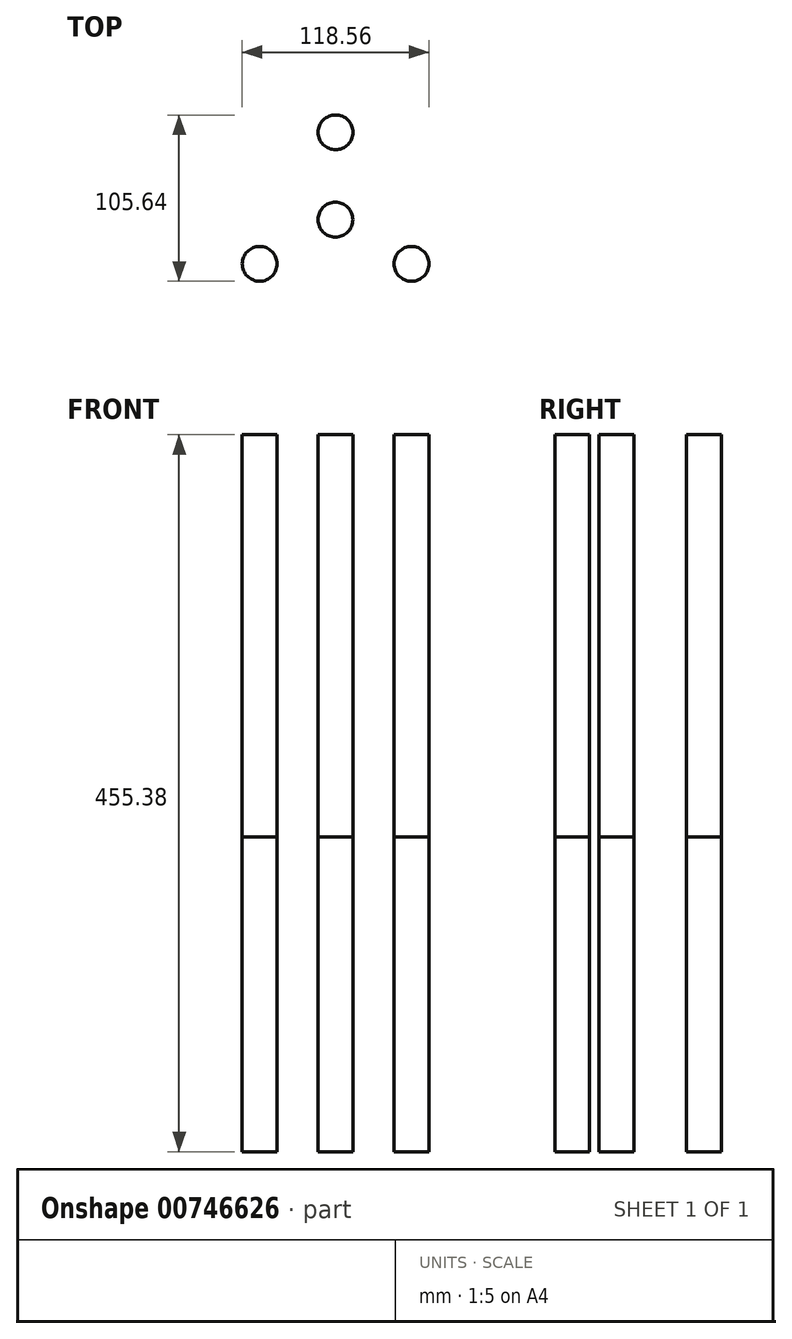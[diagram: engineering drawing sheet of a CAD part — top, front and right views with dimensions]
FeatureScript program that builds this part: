
annotation { "Feature Type Name" : "Feature", "Feature Type Description" : "" }
export const myFeature = defineFeature(function(context is Context, id is Id, definition is map)
    precondition{}
    {
        {
            var Q0;
            Q0=qCreatedBy(makeId("Top.planeOp"),FACE);
            var sketch = newSketch(context, id + "F0", { "sketchPlane" : qUnion([Q0])});
            skCircle(sketch, "E0", {"center": v(-0.1, 0.21) * mm, "radius": 11.05 * mm});
            skCircle(sketch, "E1", {"center": v(0, 55.7) * mm, "radius": 11.05 * mm});
            skCircle(sketch, "E2.1.0", {"center": v(-48.23, -27.85) * mm, "radius": 11.05 * mm});
            skCircle(sketch, "E2.2.0", {"center": v(48.23, -27.85) * mm, "radius": 11.05 * mm});
            skPoint(sketch, "E2.center", {"position": v(0, 0) * mm});
            skSolve(sketch);
        }
        {
            var Q0;
            Q0=makeQuery(id+"F0.imprint","IMPRINT",FACE,{"disambiguationData":[TD([[makeQuery(id+"F0.imprint","IMPRINT",EDGE,{"derivedFrom":sQuery(id+"F0.wireOp",EDGE,"E2.1.0")}),1.0]])]});
            var Q1;
            Q1=makeQuery(id+"F0.imprint","IMPRINT",FACE,{"disambiguationData":[TD([[makeQuery(id+"F0.imprint","IMPRINT",EDGE,{"derivedFrom":sQuery(id+"F0.wireOp",EDGE,"E0")}),1.0]])]});
            var Q2;
            Q2=makeQuery(id+"F0.imprint","IMPRINT",FACE,{"disambiguationData":[TD([[makeQuery(id+"F0.imprint","IMPRINT",EDGE,{"derivedFrom":sQuery(id+"F0.wireOp",EDGE,"E1")}),1.0]])]});
            var Q3;
            Q3=makeQuery(id+"F0.imprint","IMPRINT",FACE,{"disambiguationData":[TD([[makeQuery(id+"F0.imprint","IMPRINT",EDGE,{"derivedFrom":sQuery(id+"F0.wireOp",EDGE,"E2.2.0")}),1.0]])]});
            extrude(context, id + "F1", {"entities" : qUnion([Q0, Q1, Q2, Q3]), "depth" : 200 * mm, "offsetDistance" : 25 * mm});
        }
        {
            var Q0;
            Q0=makeQuery(id+"F1.opExtrude","CAP_FACE",FACE,{"disambiguationData":[OSD([sQuery(id+"F0.wireOp",EDGE,"E1")])],"isStart":false});
            var Q1;
            Q1=makeQuery(id+"F1.opExtrude","CAP_FACE",FACE,{"disambiguationData":[OSD([sQuery(id+"F0.wireOp",EDGE,"E0")])],"isStart":false});
            var Q2;
            Q2=makeQuery(id+"F1.opExtrude","CAP_FACE",FACE,{"disambiguationData":[OSD([sQuery(id+"F0.wireOp",EDGE,"E2.1.0")])],"isStart":false});
            var Q3;
            Q3=makeQuery(id+"F1.opExtrude","CAP_FACE",FACE,{"disambiguationData":[OSD([sQuery(id+"F0.wireOp",EDGE,"E2.2.0")])],"isStart":false});
            extrude(context, id + "F2", {"entities" : qUnion([Q0, Q1, Q2, Q3]), "endBound" : BoundingType.THROUGH_ALL, "depth" : 25 * mm, "offsetDistance" : 25 * mm});
        }
    });
